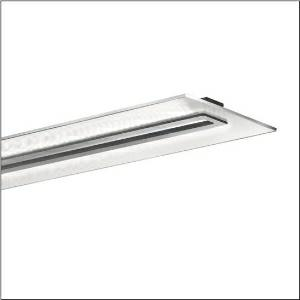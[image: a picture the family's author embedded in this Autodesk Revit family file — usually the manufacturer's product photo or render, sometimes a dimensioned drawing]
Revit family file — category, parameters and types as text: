
# Revit family: vega_11_5mn238dlc0s
name_source: partatom
category: Lighting Fixtures
units: mm (PartAtom-declared; Revit-internal decimal feet)

## family parameters
Cut with Voids When Loaded = No
Host = Face
Light Source = No
Part Type = Normal
Room Calculation Point = No
Round Connector Dimension = Use Diameter
Shared = No

## types (1)
- --- (1 x LED 4000K / CRI = 80 (unbekannt), 4300 lm, 4000K)
    Apparent Load = 31 VA
    CIE Flux Codes = 61 86 97 62 100
    Color Rendering = 80
    Color Temperature = 4000K
    Default Elevation = 1800 mm
    Description = Vega 11, office luminaire, primary light control with prismatic reflector, of PMMA, transparent prismatic structure, CAT 2 (L<= 1500cd/m²), light emission: direct/indirect distribution, primary light characteristic: symmetric, installation type: suspended mounting, surface-mounted, LED, rated luminous flux: 4.300lm, luminous efficacy: 139lm/W, light colour: 840, colour temperature: 4000K, control gear: DALI, with terminal, 3+2-pole, max. 2.5mm², mains connection: 230V, AC, 50Hz, connection cable inclusive, cable length: 1,5m, rated input power: 31W, luminaire housing, rectangular, rounded, of aluminium section, anodised, metallic grey (RAL 9006), length: 1.250mm, width: 350mm, height: 43mm, luminaire housing, lower part, of aluminium section, anodised, metallic grey (RAL 9006), of PC, grey, protection rating (complete): IP20, insulation class (complete): insulation class I (protective earthing), certification: CE, permissible operating ambient temperature: 0..+35°C, standard: EN 50419, packaging unit: 1 piece
    Height = 40 mm  [stored 0.131234 ft]
    Lamp = 1 x LED 4000K / CRI >= 80 (unbekannt)
    Lamp Light Flux = 4300 lm
    Lamp count = 1
    Length = 1250 mm
    Luminous efficacy = 139 lm/W
    Manufacturer = Siteco
    ModVariant = No
    Model = 5MN238DLC0S
    Mounting Place = Ceiling
    Mounting Type = Pendant
    Number of Poles = 1
    OnlyDefault = Yes
    Power Factor = 1
    Product Name = Vega 11
    Product group = office luminaire | ceiling pendant
    ProductGroupID = 903
    Protection Class = Protection class I
    Protection Degree = IP 20
    RLX_Detail_Level = 1
    RLX_Emergency_Light_Flux = 0 lm
    RLX_Emergency_Type = 0
    RLX_Emergency_Type_DB = No
    RlxData = <blob elided: 62813 chars, md5=f606df77>
    Socket = socket
    Standby Power = 0 W
    System Light Flux = 4300 lm
    System Power = 31 W
    Type Comments = factory setting: luminous flux: 100 % | dim-lin: 254 | 231 mA
    Type Image = l_1004807.jpg
    URL = http://relux.com
    VarID = @adj_197143
    Voltage = 0 V
    Weight = 0.00 kg
    Width = 350 mm

note: [stored X ft] marks values corroborated as IEEE doubles in the binary element streams (Revit-internal decimal feet)

## geometry (parser evidence)
native form markers: Blend x4, Sweep x10
no freeform markers — native parametric forms only
